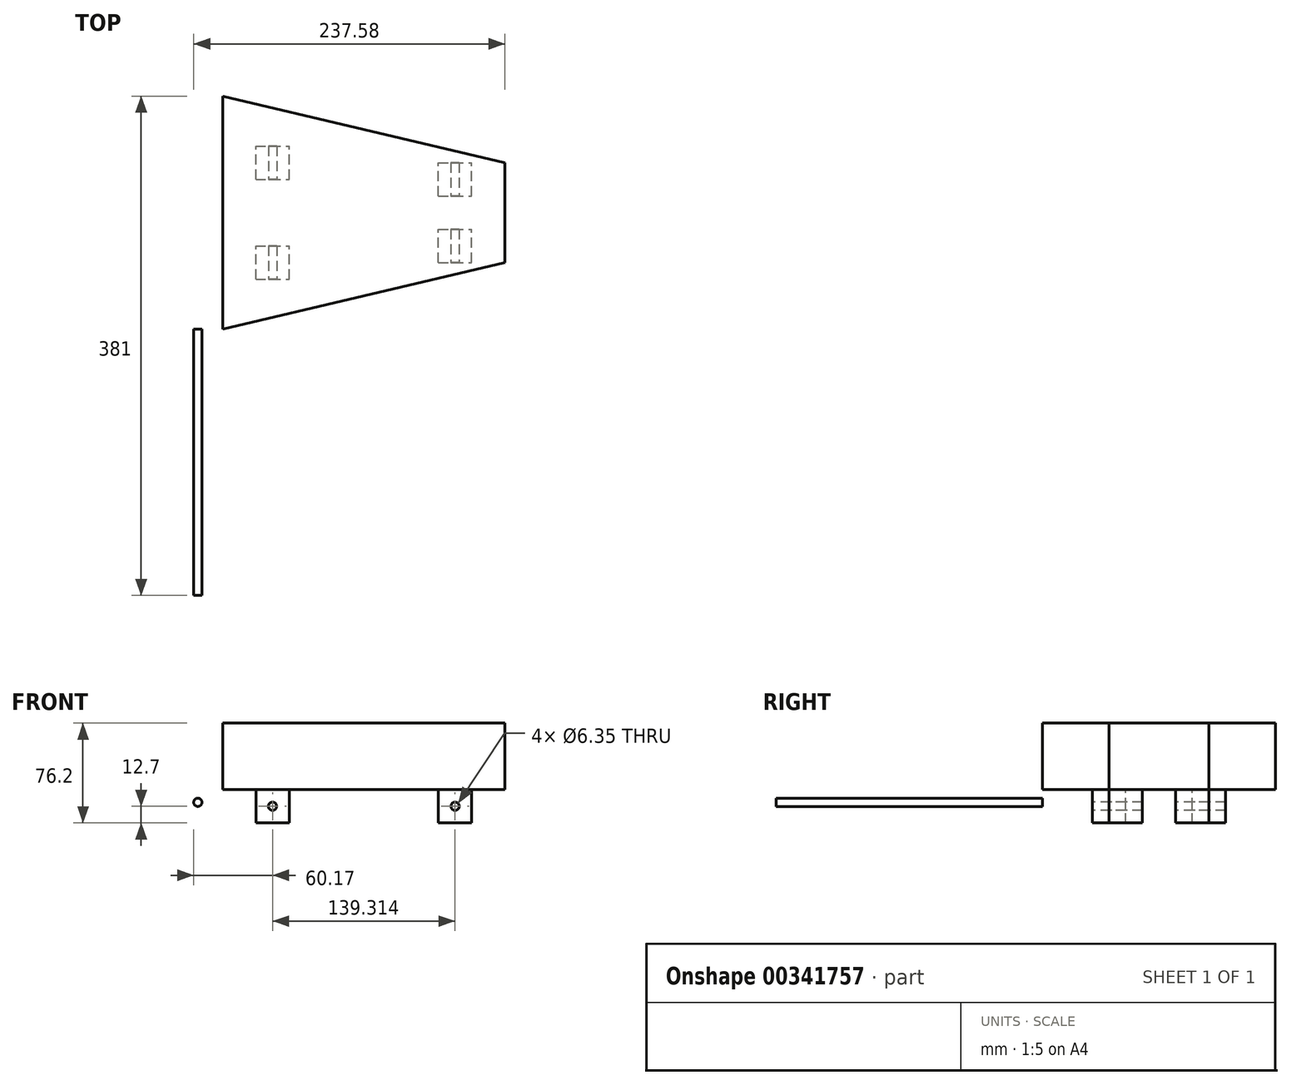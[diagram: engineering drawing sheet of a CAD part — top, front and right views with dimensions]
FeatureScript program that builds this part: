
annotation { "Feature Type Name" : "Feature", "Feature Type Description" : "" }
export const myFeature = defineFeature(function(context is Context, id is Id, definition is map)
    precondition{}
    {
        {
            var Q0;
            Q0=qCreatedBy(makeId("Top.planeOp"),FACE);
            var sketch = newSketch(context, id + "F0", { "sketchPlane" : qUnion([Q0])});
            skLineSegment(sketch, "E0", {"start": v(0, 0) * mm, "end": v(0, 177.8) * mm});
            skLineSegment(sketch, "E1", {"start": v(0, 177.8) * mm, "end": v(215.51, 127) * mm});
            skLineSegment(sketch, "E2", {"start": v(215.51, 127) * mm, "end": v(215.51, 50.8) * mm});
            skLineSegment(sketch, "E3", {"start": v(215.51, 50.8) * mm, "end": v(0, 0) * mm});
            skSolve(sketch);
        }
        {
            var Q0;
            Q0 = qSketchRegion(id + "F0", true);
            extrude(context, id + "F1", {"entities" : qUnion([Q0]), "depth" : 50.8 * mm});
        }
        {
            var Q0;
            Q0=makeQuery(id+"F1.opExtrude","CAP_FACE",FACE,{"disambiguationData":[OSD([sQuery(id+"F0.wireOp",EDGE,"E0"),sQuery(id+"F0.wireOp",EDGE,"E1"),sQuery(id+"F0.wireOp",EDGE,"E2"),sQuery(id+"F0.wireOp",EDGE,"E3")])],"isStart":true});
            var sketch = newSketch(context, id + "F2", { "sketchPlane" : qUnion([Q0])});
            skLineSegment(sketch, "E4.bottom", {"start": v(164.71, -50.8) * mm, "end": v(190.11, -50.8) * mm});
            skLineSegment(sketch, "E4.top", {"start": v(164.71, -76.2) * mm, "end": v(190.11, -76.2) * mm});
            skLineSegment(sketch, "E4.left", {"start": v(164.71, -50.8) * mm, "end": v(164.71, -76.2) * mm});
            skLineSegment(sketch, "E4.right", {"start": v(190.11, -50.8) * mm, "end": v(190.11, -76.2) * mm});
            skLineSegment(sketch, "E5.bottom", {"start": v(164.71, -101.6) * mm, "end": v(190.11, -101.6) * mm});
            skLineSegment(sketch, "E5.top", {"start": v(164.71, -127) * mm, "end": v(190.11, -127) * mm});
            skLineSegment(sketch, "E5.left", {"start": v(164.71, -101.6) * mm, "end": v(164.71, -127) * mm});
            skLineSegment(sketch, "E5.right", {"start": v(190.11, -101.6) * mm, "end": v(190.11, -127) * mm});
            skLineSegment(sketch, "E6.bottom", {"start": v(25.4, -38.1) * mm, "end": v(50.8, -38.1) * mm});
            skLineSegment(sketch, "E6.top", {"start": v(25.4, -63.5) * mm, "end": v(50.8, -63.5) * mm});
            skLineSegment(sketch, "E6.left", {"start": v(25.4, -38.1) * mm, "end": v(25.4, -63.5) * mm});
            skLineSegment(sketch, "E6.right", {"start": v(50.8, -38.1) * mm, "end": v(50.8, -63.5) * mm});
            skLineSegment(sketch, "E7.bottom", {"start": v(25.4, -114.3) * mm, "end": v(50.8, -114.3) * mm});
            skLineSegment(sketch, "E7.top", {"start": v(25.4, -139.7) * mm, "end": v(50.8, -139.7) * mm});
            skLineSegment(sketch, "E7.left", {"start": v(25.4, -114.3) * mm, "end": v(25.4, -139.7) * mm});
            skLineSegment(sketch, "E7.right", {"start": v(50.8, -114.3) * mm, "end": v(50.8, -139.7) * mm});
            skSolve(sketch);
        }
        {
            var Q0;
            Q0 = qSketchRegion(id + "F2", true);
            extrude(context, id + "F3", {"entities" : qUnion([Q0]), "operationType" : NewBodyOperationType.ADD, "depth" : 25.4 * mm});
        }
        {
            var Q0;
            Q0=qCreatedBy(makeId("Front.planeOp"),FACE);
            var sketch = newSketch(context, id + "F4", { "sketchPlane" : qUnion([Q0])});
            skCircle(sketch, "E8", {"center": v(38.1, -12.7) * mm, "radius": 3.18 * mm});
            skCircle(sketch, "E9", {"center": v(177.41, -12.7) * mm, "radius": 3.18 * mm});
            skSolve(sketch);
        }
        {
            var Q0;
            Q0 = qSketchRegion(id + "F4", true);
            extrude(context, id + "F5", {"entities" : qUnion([Q0]), "operationType" : NewBodyOperationType.REMOVE, "endBound" : BoundingType.THROUGH_ALL, "oppositeDirection" : true, "depth" : 25.4 * mm});
        }
        {
            var Q0;
            Q0=qCreatedBy(makeId("Front.planeOp"),FACE);
            var sketch = newSketch(context, id + "F6", { "sketchPlane" : qUnion([Q0])});
            skCircle(sketch, "E10", {"center": v(-18.9, -9.69) * mm, "radius": 3.17 * mm});
            skSolve(sketch);
        }
        {
            var Q0;
            Q0 = qSketchRegion(id + "F6", true);
            extrude(context, id + "F7", {"entities" : qUnion([Q0]), "depth" : 203.2 * mm});
        }
    });
